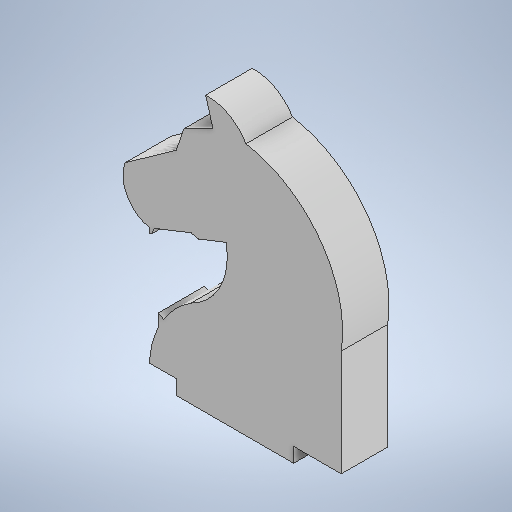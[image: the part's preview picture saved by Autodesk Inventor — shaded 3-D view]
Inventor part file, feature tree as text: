
AUTODESK INVENTOR PART (.ipt)
format: ipt  version: 2025.1 (Build 291241000, 241)  size: 302,592 bytes
history: native  units: mm
features: other x2, extrude x1, sketch x1
ambient origin geometry x8: Origin, YZ Plane, XZ Plane, XY Plane, X Axis, Y Axis, Z Axis, Center Point
bodies: Body1 (feature_tree)
feature tree (4):
  other  "Sólido1"
  extrude  "Extrusión1"  Depth=10.0mm
  sketch  "Boceto1"  dims[d5=10.0mm d6=0.0mm d8=14.0mm]
  other  "Imagen1"
